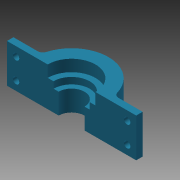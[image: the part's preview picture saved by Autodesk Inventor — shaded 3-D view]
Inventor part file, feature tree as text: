
AUTODESK INVENTOR PART (.ipt)
format: ipt  version: 2015 (Build 190159000, 159)  size: 133,120 bytes
history: native  units: mm
features: extrude x5, sketch x5, fillet x1
ambient origin geometry x8: Origin, YZ Plane, XZ Plane, XY Plane, X Axis, Y Axis, Z Axis, Center Point
bodies: 实体1 (feature_tree)
feature tree (11):
  extrude  "拉伸1"  Depth=100.0mm
  extrude  "拉伸2"  Depth=30.0mm TaperAngle=0.0deg
  extrude  "拉伸3"  Depth=9.0mm TaperAngle=0.0deg
  extrude  "拉伸4"  Depth=5.0mm TaperAngle=0.0deg
  fillet  "圆角1"  Radius=20.0mm
  extrude  "拉伸5"  Depth=4.0mm
  sketch  "草图1"  dims[d0=57.0mm d1=100.0mm]
  sketch  "草图2"  dims[d2=5.0mm d3=30.0mm d4=0.0mm]
  sketch  "草图3"  dims[d5=37.0mm d6=9.0mm d7=0.0mm]
  sketch  "草图4"  dims[d8=28.0mm d9=5.0mm d10=0.0mm d11=20.0mm]
  sketch  "草图5"  dims[d12=5.0mm d13=0.0mm d14=4.0mm d15=5.0mm d16=5.0mm d17=5.0mm d18=5.0mm d19=7.0mm d20=7.0mm d21=7.0mm d22=7.0mm d23=7.0mm d24=7.0mm d25=7.0mm d26=7.0mm d27=5.0mm d28=0.0mm]
